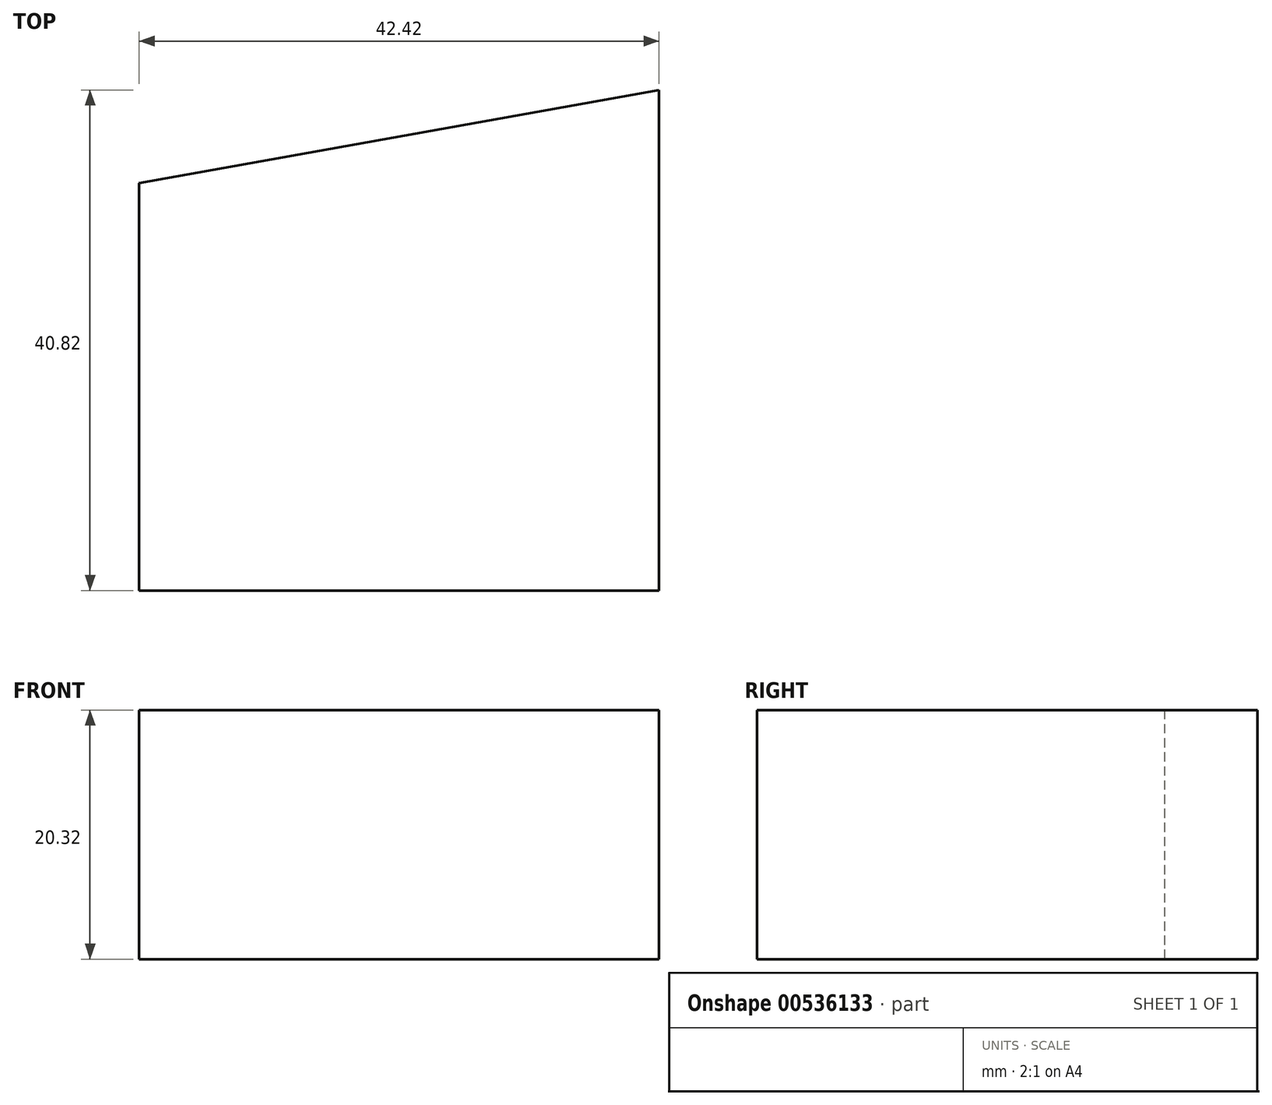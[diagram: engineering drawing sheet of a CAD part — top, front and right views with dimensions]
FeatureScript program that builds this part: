
annotation { "Feature Type Name" : "Feature", "Feature Type Description" : "" }
export const myFeature = defineFeature(function(context is Context, id is Id, definition is map)
    precondition{}
    {
        {
            var Q0;
            Q0=qCreatedBy(makeId("Top.planeOp"),FACE);
            var sketch = newSketch(context, id + "F0", { "sketchPlane" : qUnion([Q0])});
            skLineSegment(sketch, "E0", {"start": v(0, 0) * mm, "end": v(42.42, 0) * mm});
            skLineSegment(sketch, "E1", {"start": v(42.42, 0) * mm, "end": v(42.42, 40.82) * mm});
            skLineSegment(sketch, "E2", {"start": v(42.42, 40.82) * mm, "end": v(0, 33.23) * mm});
            skLineSegment(sketch, "E3", {"start": v(0, 33.23) * mm, "end": v(0, 0) * mm});
            skSolve(sketch);
        }
        {
            var Q0;
            Q0 = qSketchRegion(id + "F0", true);
            extrude(context, id + "F1", {"entities" : qUnion([Q0]), "depth" : 20.32 * mm, "offsetDistance" : 25.4 * mm});
        }
    });
